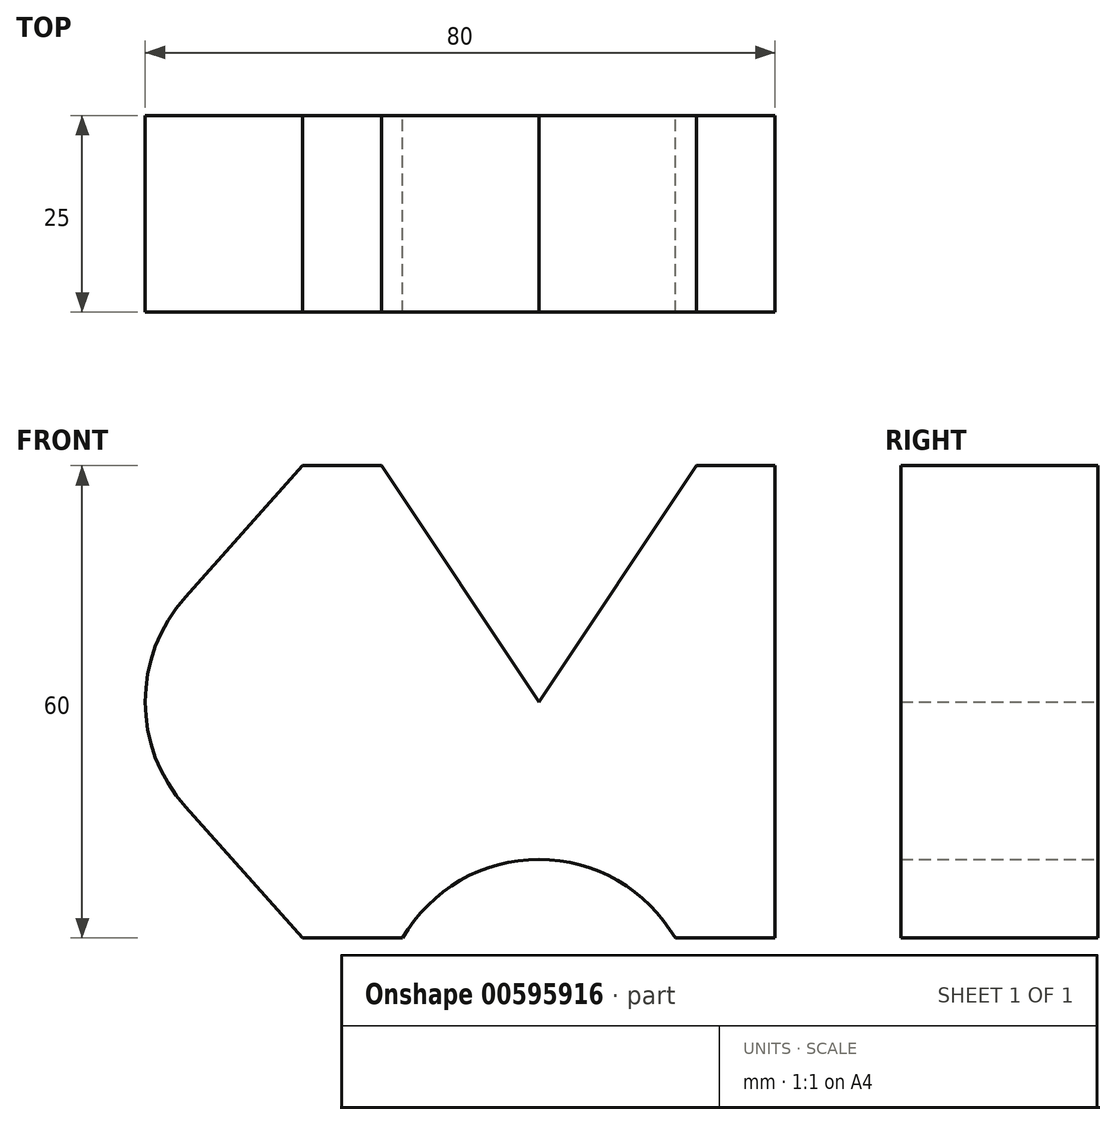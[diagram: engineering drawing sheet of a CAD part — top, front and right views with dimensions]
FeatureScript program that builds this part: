
annotation { "Feature Type Name" : "Feature", "Feature Type Description" : "" }
export const myFeature = defineFeature(function(context is Context, id is Id, definition is map)
    precondition{}
    {
        {
            var Q0;
            Q0=qCreatedBy(makeId("Front.planeOp"),FACE);
            var sketch = newSketch(context, id + "F0", { "sketchPlane" : qUnion([Q0])});
            skLineSegment(sketch, "E0", {"start": v(0, 0) * mm, "end": v(20, 30) * mm});
            skLineSegment(sketch, "E1", {"start": v(20, 30) * mm, "end": v(30, 30) * mm});
            skLineSegment(sketch, "E2", {"start": v(30, 30) * mm, "end": v(30, -30) * mm});
            skLineSegment(sketch, "E3", {"start": v(30, -30) * mm, "end": v(17.32, -30) * mm});
            skArc(sketch, "E4", {"start": v(17.32, -30) * mm, "mid": v(0, -20) * mm, "end": v(-17.32, -30) * mm});
            skLineSegment(sketch, "E5", {"start": v(-17.32, -30) * mm, "end": v(-30, -30) * mm});
            skLineSegment(sketch, "E6", {"start": v(-30, -30) * mm, "end": v(-44.9, -13.33) * mm});
            skArc(sketch, "E7", {"start": v(-44.9, 13.33) * mm, "mid": v(-50, 0) * mm, "end": v(-44.9, -13.33) * mm});
            skLineSegment(sketch, "E8", {"start": v(-44.9, 13.33) * mm, "end": v(-30, 30) * mm});
            skLineSegment(sketch, "E9", {"start": v(-30, 30) * mm, "end": v(-20, 30) * mm});
            skLineSegment(sketch, "E10", {"start": v(-20, 30) * mm, "end": v(0, 0) * mm});
            skLineSegment(sketch, "E11", {"start": v(-69.02, 0) * mm, "end": v(69.22, 0) * mm, "construction": true});
            skLineSegment(sketch, "E12", {"start": v(-30, 30) * mm, "end": v(-30, -30) * mm, "construction": true});
            skSolve(sketch);
        }
        {
            var Q0;
            Q0=makeQuery(id+"F0.imprint","IMPRINT",FACE,{"disambiguationData":[TD([[makeQuery(id+"F0.imprint","IMPRINT",EDGE,{"derivedFrom":sQuery(id+"F0.wireOp",EDGE,"E0")}),-1.0]])]});
            extrude(context, id + "F1", {"entities" : qUnion([Q0]), "depth" : 25 * mm, "offsetDistance" : 25 * mm});
        }
    });
